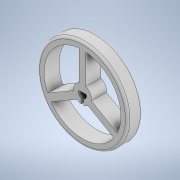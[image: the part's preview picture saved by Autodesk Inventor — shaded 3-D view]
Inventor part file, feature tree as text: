
AUTODESK INVENTOR PART (.ipt)
format: ipt  version: 2022.2 (Build 262287010, 287A)  size: 186,880 bytes
history: native  units: mm
features: extrude x4, sketch x4, fillet x1
ambient origin geometry x8: Origin, YZ Plane, XZ Plane, XY Plane, X Axis, Y Axis, Z Axis, Center Point
bodies: Solid1 (feature_tree)
feature tree (9):
  extrude  "Extrusion1"  Depth=6.6mm TaperAngle=0.0deg
  extrude  "Extrusion3"  TaperAngle=120.0deg  [1 undecoded]
  extrude  "Extrusion5"  Depth=1.5mm
  extrude  "Extrusion6"  Depth=1.0mm
  fillet  "Arredondamento1"  Radius=1.5mm
  sketch  "Sketch1"  dims[d0=40.0mm d1=6.6mm d2=0.0mm]
  sketch  "Sketch3"  dims[d6=34.0mm d7=120.0deg]
  sketch  "Sketch5"  dims[d8=150.0deg d9=1.5mm]
  sketch  "Sketch6"  dims[d10=1.5mm d11=1.5mm d12=1.5mm d13=1.5mm d14=1.5mm d15=2.0mm d16=0.0mm d20=8.0mm d21=6.6mm d22=0.0mm d23=3.5mm d24=0.5mm d25=0.5mm d27=10.0mm d28=0.0mm d29=2.5mm d30=1.0mm d26=0.5mm]
note: 1 required parameter value undecoded (feature->parameter linkage not recoverable at this tier; creation-order binding heuristic only, values carry confidence <= 0.55)
